# Revit family: 318_4eea458b4f7e42a1ac5290e23d8493
name_source: partatom
category: Pipe Accessories
units: mm (PartAtom-declared; Revit-internal decimal feet)

## family parameters
Always vertical = Yes
Cut with Voids When Loaded = No
Part Type = Valve - Normal
Round Connector Dimension = Use Diameter
Shared = No
Work Plane-Based = No

## types (1)
- GMA231  INCL. SEPARATOR
    BL = 450 mm  [stored 1.47638 ft]
    BL1 = 225 mm  [stored 0.738189 ft]
    BW = 160 mm  [stored 0.524934 ft]
    BW1 = 8 mm  [stored 0.0262467 ft]
    BW11 = 145 mm  [stored 0.475722 ft]
    BW11__ve = -145 mm  [stored -0.475722 ft]
    C = 125 mm  [stored 0.410105 ft]
    C2 = 88 mm
    CAT0 = Yes
    CC = 570 mm  [stored 1.87008 ft]
    CC2 = 285 mm  [stored 0.935039 ft]
    CenSd_NR_6 = 22 mm
    Description = Manifold GMA231 for 3 units, PN4 with hydraulic separator
    L = 800 mm  [stored 2.62467 ft]
    LX = 400 mm  [stored 1.31234 ft]
    MP1 = 32 mm
    MP3 = 32 mm
    Manufacturer = ESBE
    NR = 25 mm  [stored 0.082021 ft]
    QmdConnectorList = 321;MP1;322;SBP1;323;SBP2;324;SBP3;351;MP3;352;RBP1;353;RBP2;354;RBP3
    RBP1 = 32 mm
    RBP2 = 32 mm
    RBP3 = 32 mm
    RR = 16 mm  [stored 0.0524934 ft]
    RRB1 = 16 mm  [stored 0.0524934 ft]
    RRB2 = 16 mm  [stored 0.0524934 ft]
    RRB3 = 16 mm  [stored 0.0524934 ft]
    RS = 16 mm  [stored 0.0524934 ft]
    RSB1 = 16 mm  [stored 0.0524934 ft]
    RSB2 = 16 mm  [stored 0.0524934 ft]
    RSB3 = 16 mm  [stored 0.0524934 ft]
    SBP1 = 32 mm
    SBP2 = 32 mm
    SBP3 = 32 mm
    URL = http://www.esbe.eu
    W = 170 mm  [stored 0.557743 ft]
    W2 = 245 mm  [stored 0.803806 ft]
    WB = 15 mm  [stored 0.0492126 ft]
    XB = 40 mm
    XB1 = 24 mm
    ZP = 20 mm  [stored 0.0656168 ft]
    ZP0 = 5 mm  [stored 0.0164042 ft]
    ZP1 = 145 mm  [stored 0.475722 ft]
    magiPartTypeId = 318
    magiProductCode = GMA231  INCL. SEPARATOR
    magiProductFamilyId = 4eea458b4f7e42a1ac5290e23d8493
    magiProductId = 4eea458b4f7e42a1ac5290e23d8493

note: [stored X ft] marks values corroborated as IEEE doubles in the binary element streams (Revit-internal decimal feet)

## geometry (parser evidence)
native form markers: Sweep x3
no freeform markers — native parametric forms only
